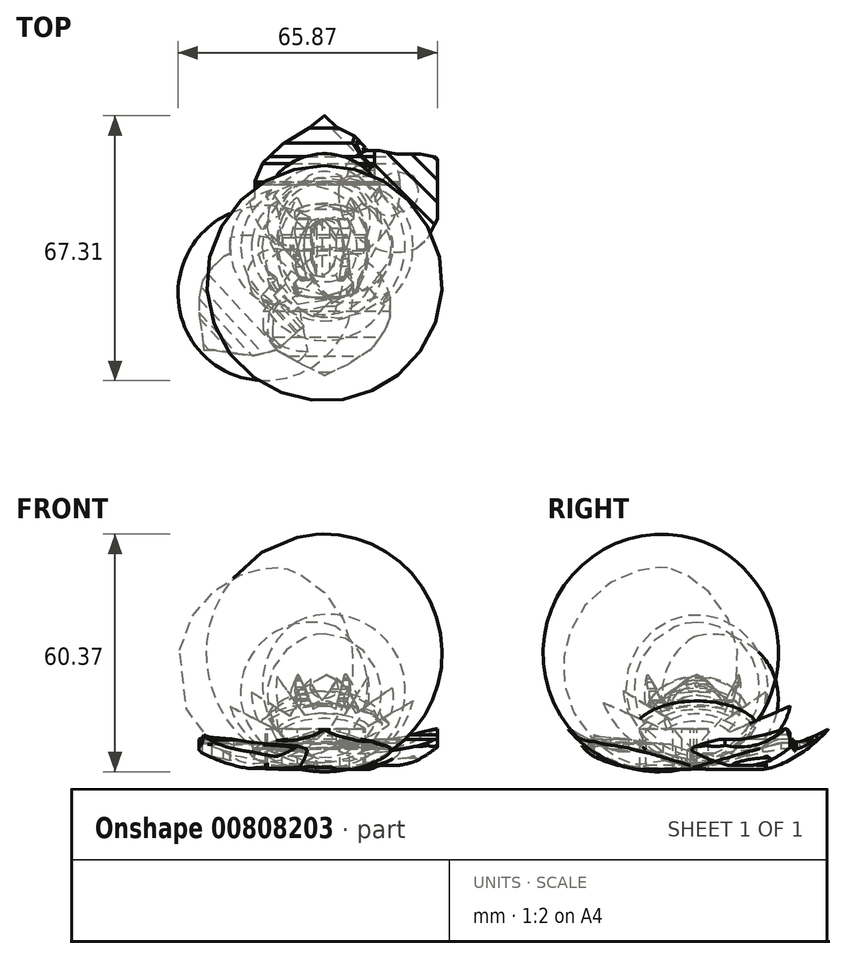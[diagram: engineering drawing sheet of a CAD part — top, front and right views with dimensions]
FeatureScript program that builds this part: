
annotation { "Feature Type Name" : "Feature", "Feature Type Description" : "" }
export const myFeature = defineFeature(function(context is Context, id is Id, definition is map)
    precondition{}
    {
        {
            var Q0;
            Q0=qCreatedBy(makeId("Front.planeOp"),FACE);
            var sketch = newSketch(context, id + "F0", { "sketchPlane" : qUnion([Q0])});
            skLineSegment(sketch, "E0", {"start": v(0, 14.2) * mm, "end": v(0, -5.34) * mm});
            skArc(sketch, "E1", {"start": v(0, -5.34) * mm, "mid": v(7.6, 4.43) * mm, "end": v(0, 14.2) * mm});
            skSolve(sketch);
        }
        {
            var Q0;
            Q0 = qSketchRegion(id + "F0", true);
            var Q1;
            Q1=sQuery(id+"F0.wireOp",EDGE,"E0");
            revolve(context, id + "F1", {"surfaceOperationType" : NewSurfaceOperationType.NEW, "entities" : qUnion([Q0]), "axis" : qUnion([Q1]), "revolveType" : RevolveType.FULL});
        }
        {
            var Q0;
            Q0=qCreatedBy(makeId("Front.planeOp"),FACE);
            var sketch = newSketch(context, id + "F2", { "sketchPlane" : qUnion([Q0])});
            skLineSegment(sketch, "E2", {"start": v(-1.74, 15.97) * mm, "end": v(-3.4, 13.54) * mm});
            skLineSegment(sketch, "E3", {"start": v(-3.4, 13.54) * mm, "end": v(-3.4, 11.38) * mm});
            skLineSegment(sketch, "E4", {"start": v(-3.4, 11.38) * mm, "end": v(-0.63, 7.29) * mm});
            skLineSegment(sketch, "E5", {"start": v(-0.63, 7.29) * mm, "end": v(1.25, 9.5) * mm});
            skLineSegment(sketch, "E6", {"start": v(1.25, 9.5) * mm, "end": v(2.98, 12.29) * mm});
            skLineSegment(sketch, "E7", {"start": v(2.98, 12.29) * mm, "end": v(2.98, 13.88) * mm});
            skLineSegment(sketch, "E8", {"start": v(2.98, 13.88) * mm, "end": v(2.29, 15.97) * mm});
            skLineSegment(sketch, "E9", {"start": v(2.29, 15.97) * mm, "end": v(-1.74, 15.97) * mm});
            skSolve(sketch);
        }
        {
            var Q0;
            Q0 = qSketchRegion(id + "F2", true);
            extrude(context, id + "F3", {"entities" : qUnion([Q0]), "operationType" : NewBodyOperationType.REMOVE, "oppositeDirection" : true, "depth" : 25.4 * mm, "offsetDistance" : 25.4 * mm});
        }
        {
            var Q0;
            Q0 = qSketchRegion(id + "F2", true);
            extrude(context, id + "F4", {"entities" : qUnion([Q0]), "operationType" : NewBodyOperationType.REMOVE, "depth" : 25.4 * mm, "offsetDistance" : 25.4 * mm});
        }
        {
            var Q0;
            Q0=qCreatedBy(makeId("Front.planeOp"),FACE);
            var sketch = newSketch(context, id + "F5", { "sketchPlane" : qUnion([Q0])});
            skLineSegment(sketch, "E10", {"start": v(2.63, 4.43) * mm, "end": v(8.5, 2.9) * mm});
            skArc(sketch, "E11", {"start": v(8.5, 2.9) * mm, "mid": v(8.02, 8.9) * mm, "end": v(5.25, 14.26) * mm});
            skLineSegment(sketch, "E12", {"start": v(5.25, 14.26) * mm, "end": v(2.63, 4.43) * mm});
            skSolve(sketch);
        }
        {
            var Q0;
            Q0 = qSketchRegion(id + "F5", true);
            var Q1;
            Q1=sQuery(id+"F5.wireOp",EDGE,"E10");
            revolve(context, id + "F6", {"operationType" : NewBodyOperationType.ADD, "surfaceOperationType" : NewSurfaceOperationType.NEW, "entities" : qUnion([Q0]), "axis" : qUnion([Q1]), "revolveType" : RevolveType.FULL});
        }
        {
            var Q0;
            Q0=qCreatedBy(makeId("Front.planeOp"),FACE);
            var sketch = newSketch(context, id + "F7", { "sketchPlane" : qUnion([Q0])});
            skLineSegment(sketch, "E13", {"start": v(-6.7, 13.9) * mm, "end": v(-1.32, 3.83) * mm});
            skLineSegment(sketch, "E14", {"start": v(-1.32, 3.83) * mm, "end": v(-7.78, 1.4) * mm});
            skArc(sketch, "E15", {"start": v(-6.7, 13.9) * mm, "mid": v(-8.72, 7.78) * mm, "end": v(-7.78, 1.4) * mm});
            skSolve(sketch);
        }
        {
            var Q0;
            Q0 = qSketchRegion(id + "F7", true);
            var Q1;
            Q1=sQuery(id+"F7.wireOp",EDGE,"E14");
            revolve(context, id + "F8", {"operationType" : NewBodyOperationType.ADD, "surfaceOperationType" : NewSurfaceOperationType.NEW, "entities" : qUnion([Q0]), "axis" : qUnion([Q1]), "revolveType" : RevolveType.FULL});
        }
        {
            var Q0;
            Q0=qCreatedBy(makeId("Front.planeOp"),FACE);
            var sketch = newSketch(context, id + "F9", { "sketchPlane" : qUnion([Q0])});
            skLineSegment(sketch, "E16", {"start": v(3.45, -3.75) * mm, "end": v(0, -5.55) * mm});
            skLineSegment(sketch, "E17", {"start": v(0, -5.55) * mm, "end": v(-1.31, -5.1) * mm});
            skLineSegment(sketch, "E18", {"start": v(-1.31, -5.1) * mm, "end": v(-2.95, -4.56) * mm});
            skLineSegment(sketch, "E19", {"start": v(-2.95, -4.56) * mm, "end": v(-4.9, -3.61) * mm});
            skLineSegment(sketch, "E20", {"start": v(-4.9, -3.61) * mm, "end": v(-4.41, -5.72) * mm});
            skLineSegment(sketch, "E21", {"start": v(-4.41, -5.72) * mm, "end": v(1, -7.97) * mm});
            skLineSegment(sketch, "E22", {"start": v(1, -7.97) * mm, "end": v(3.45, -3.75) * mm});
            skSolve(sketch);
        }
        {
            var Q0;
            Q0 = qSketchRegion(id + "F9", true);
            extrude(context, id + "F10", {"entities" : qUnion([Q0]), "operationType" : NewBodyOperationType.REMOVE, "oppositeDirection" : true, "depth" : 25.4 * mm, "offsetDistance" : 25.4 * mm});
        }
        {
            var Q0;
            Q0 = qSketchRegion(id + "F9", true);
            extrude(context, id + "F11", {"entities" : qUnion([Q0]), "operationType" : NewBodyOperationType.REMOVE, "depth" : 25.4 * mm, "offsetDistance" : 25.4 * mm});
        }
        {
            var Q0;
            Q0=qCreatedBy(makeId("Right.planeOp"),FACE);
            var sketch = newSketch(context, id + "F12", { "sketchPlane" : qUnion([Q0])});
            skLineSegment(sketch, "E23", {"start": v(0, -5.52) * mm, "end": v(-12.6, 14.04) * mm});
            skLineSegment(sketch, "E24", {"start": v(-12.6, 14.04) * mm, "end": v(-5.19, 2.53) * mm});
            skLineSegment(sketch, "E25", {"start": v(-5.19, 2.53) * mm, "end": v(-11.6, 0) * mm});
            skArc(sketch, "E26", {"start": v(-12.6, 14.04) * mm, "mid": v(-13.1, 6.95) * mm, "end": v(-11.6, 0) * mm});
            skSolve(sketch);
        }
        {
            var Q0;
            Q0=qCreatedBy(makeId("Right.planeOp"),FACE);
            var sketch = newSketch(context, id + "F13", { "sketchPlane" : qUnion([Q0])});
            skLineSegment(sketch, "E27", {"start": v(0.52, 17) * mm, "end": v(1.55, 15.39) * mm});
            skLineSegment(sketch, "E28", {"start": v(1.55, 15.39) * mm, "end": v(4.15, 13.96) * mm});
            skLineSegment(sketch, "E29", {"start": v(4.15, 13.96) * mm, "end": v(8.05, 11.22) * mm});
            skLineSegment(sketch, "E30", {"start": v(8.05, 11.22) * mm, "end": v(9.5, 7.76) * mm});
            skLineSegment(sketch, "E31", {"start": v(9.5, 7.76) * mm, "end": v(9.5, 5.02) * mm});
            skLineSegment(sketch, "E32", {"start": v(9.5, 5.02) * mm, "end": v(9.5, 2.03) * mm});
            skLineSegment(sketch, "E33", {"start": v(9.5, 2.03) * mm, "end": v(8.62, 0) * mm});
            skLineSegment(sketch, "E34", {"start": v(8.62, 0) * mm, "end": v(6.68, -2.62) * mm});
            skLineSegment(sketch, "E35", {"start": v(6.68, -2.62) * mm, "end": v(1.83, -5.49) * mm});
            skLineSegment(sketch, "E36", {"start": v(1.83, -5.49) * mm, "end": v(0.67, -5.49) * mm});
            skLineSegment(sketch, "E37", {"start": v(0.67, -5.49) * mm, "end": v(5.65, -6.91) * mm});
            skLineSegment(sketch, "E38", {"start": v(5.65, -6.91) * mm, "end": v(12.66, -3.5) * mm});
            skLineSegment(sketch, "E39", {"start": v(12.66, -3.5) * mm, "end": v(12.66, 2.12) * mm});
            skLineSegment(sketch, "E40", {"start": v(12.66, 2.12) * mm, "end": v(11.25, 16) * mm});
            skLineSegment(sketch, "E41", {"start": v(11.25, 16) * mm, "end": v(0.52, 17) * mm});
            skSolve(sketch);
        }
        {
            var Q0;
            Q0 = qSketchRegion(id + "F13", true);
            extrude(context, id + "F14", {"entities" : qUnion([Q0]), "operationType" : NewBodyOperationType.REMOVE, "depth" : 25.4 * mm, "offsetDistance" : 25.4 * mm});
        }
        {
            var Q0;
            Q0 = qSketchRegion(id + "F13", true);
            extrude(context, id + "F15", {"entities" : qUnion([Q0]), "operationType" : NewBodyOperationType.REMOVE, "oppositeDirection" : true, "depth" : 25.4 * mm, "offsetDistance" : 25.4 * mm});
        }
        {
            var Q0;
            Q0=qCreatedBy(makeId("Right.planeOp"),FACE);
            var sketch = newSketch(context, id + "F16", { "sketchPlane" : qUnion([Q0])});
            skLineSegment(sketch, "E42", {"start": v(0, 14.33) * mm, "end": v(3.36, 12.86) * mm});
            skLineSegment(sketch, "E43", {"start": v(3.36, 12.86) * mm, "end": v(5.83, 10.3) * mm});
            skLineSegment(sketch, "E44", {"start": v(5.83, 10.3) * mm, "end": v(7.11, 7.74) * mm});
            skLineSegment(sketch, "E45", {"start": v(7.11, 7.74) * mm, "end": v(8.3, 4.27) * mm});
            skLineSegment(sketch, "E46", {"start": v(8.3, 4.27) * mm, "end": v(6.93, 0.98) * mm});
            skLineSegment(sketch, "E47", {"start": v(6.93, 0.98) * mm, "end": v(5, -1.22) * mm});
            skLineSegment(sketch, "E48", {"start": v(5, -1.22) * mm, "end": v(1.17, -5.06) * mm});
            skLineSegment(sketch, "E49", {"start": v(1.17, -5.06) * mm, "end": v(0, -6.16) * mm});
            skLineSegment(sketch, "E50", {"start": v(0, -6.16) * mm, "end": v(3.18, -7.71) * mm});
            skLineSegment(sketch, "E51", {"start": v(3.18, -7.71) * mm, "end": v(12.6, 0) * mm});
            skLineSegment(sketch, "E52", {"start": v(12.6, 0) * mm, "end": v(12.6, 9.2) * mm});
            skLineSegment(sketch, "E53", {"start": v(12.6, 9.2) * mm, "end": v(8.12, 14.14) * mm});
            skLineSegment(sketch, "E54", {"start": v(8.12, 14.14) * mm, "end": v(0, 14.33) * mm});
            skSolve(sketch);
        }
        {
            var Q0;
            Q0 = qSketchRegion(id + "F16", true);
            extrude(context, id + "F17", {"entities" : qUnion([Q0]), "operationType" : NewBodyOperationType.REMOVE, "oppositeDirection" : true, "depth" : 25.4 * mm, "offsetDistance" : 25.4 * mm});
        }
        {
            var Q0;
            Q0 = qSketchRegion(id + "F16", true);
            extrude(context, id + "F18", {"entities" : qUnion([Q0]), "operationType" : NewBodyOperationType.REMOVE, "depth" : 25.4 * mm, "offsetDistance" : 25.4 * mm});
        }
        {
            var Q0;
            Q0=qCreatedBy(makeId("Right.planeOp"),FACE);
            var sketch = newSketch(context, id + "F19", { "sketchPlane" : qUnion([Q0])});
            skLineSegment(sketch, "E55", {"start": v(0, 14.92) * mm, "end": v(-4.7, 12.16) * mm});
            skLineSegment(sketch, "E56", {"start": v(-4.7, 12.16) * mm, "end": v(-7.9, 8.97) * mm});
            skLineSegment(sketch, "E57", {"start": v(-7.9, 8.97) * mm, "end": v(-8.9, 6.06) * mm});
            skLineSegment(sketch, "E58", {"start": v(-8.9, 6.06) * mm, "end": v(-8.9, 1.85) * mm});
            skLineSegment(sketch, "E59", {"start": v(-8.9, 1.85) * mm, "end": v(-7.3, -1.78) * mm});
            skLineSegment(sketch, "E60", {"start": v(-7.3, -1.78) * mm, "end": v(-3.53, -5.7) * mm});
            skLineSegment(sketch, "E61", {"start": v(-3.53, -5.7) * mm, "end": v(-1.5, -6.86) * mm});
            skLineSegment(sketch, "E62", {"start": v(-1.5, -6.86) * mm, "end": v(-6.3, -10.64) * mm});
            skLineSegment(sketch, "E63", {"start": v(-6.3, -10.64) * mm, "end": v(-15.88, -2.5) * mm});
            skLineSegment(sketch, "E64", {"start": v(-15.88, -2.5) * mm, "end": v(-15.88, 6.06) * mm});
            skLineSegment(sketch, "E65", {"start": v(-15.88, 6.06) * mm, "end": v(-5.86, 16.08) * mm});
            skLineSegment(sketch, "E66", {"start": v(-5.86, 16.08) * mm, "end": v(0, 14.92) * mm});
            skSolve(sketch);
        }
        {
            var Q0;
            Q0 = qSketchRegion(id + "F19", true);
            extrude(context, id + "F20", {"entities" : qUnion([Q0]), "operationType" : NewBodyOperationType.REMOVE, "oppositeDirection" : true, "depth" : 25.4 * mm, "offsetDistance" : 25.4 * mm});
        }
        {
            var Q0;
            Q0 = qSketchRegion(id + "F19", true);
            extrude(context, id + "F21", {"entities" : qUnion([Q0]), "operationType" : NewBodyOperationType.REMOVE, "depth" : 25.4 * mm, "offsetDistance" : 25.4 * mm});
        }
        {
            var Q0;
            Q0=qCreatedBy(makeId("Right.planeOp"),FACE);
            var sketch = newSketch(context, id + "F22", { "sketchPlane" : qUnion([Q0])});
            skLineSegment(sketch, "E67", {"start": v(0, 14.3) * mm, "end": v(0, 13.37) * mm});
            skLineSegment(sketch, "E68", {"start": v(4.66, 10.12) * mm, "end": v(7.1, 7.8) * mm});
            skLineSegment(sketch, "E69", {"start": v(7.1, 7.8) * mm, "end": v(9.19, 6.75) * mm});
            skLineSegment(sketch, "E70", {"start": v(9.19, 6.75) * mm, "end": v(4.78, 22.54) * mm});
            skLineSegment(sketch, "E71", {"start": v(-7.42, 16.04) * mm, "end": v(-10.43, 7.33) * mm});
            skLineSegment(sketch, "E72", {"start": v(-10.43, 7.33) * mm, "end": v(-7.65, 8.96) * mm});
            skLineSegment(sketch, "E73", {"start": v(4.66, 10.12) * mm, "end": v(2.6, 12.38) * mm});
            skLineSegment(sketch, "E74", {"start": v(2.6, 12.38) * mm, "end": v(1.43, 13.03) * mm});
            skLineSegment(sketch, "E75", {"start": v(1.43, 13.03) * mm, "end": v(0, 13.83) * mm});
            skLineSegment(sketch, "E76", {"start": v(0, 13.83) * mm, "end": v(-1.9, 12.9) * mm});
            skLineSegment(sketch, "E77", {"start": v(-1.9, 12.9) * mm, "end": v(-3.08, 12.3) * mm});
            skLineSegment(sketch, "E78", {"start": v(-3.08, 12.3) * mm, "end": v(-4.97, 10.7) * mm});
            skLineSegment(sketch, "E79", {"start": v(-4.97, 10.7) * mm, "end": v(-7.65, 8.96) * mm});
            skLineSegment(sketch, "E80", {"start": v(4.78, 22.54) * mm, "end": v(-7.42, 16.04) * mm});
            skSolve(sketch);
        }
        {
            var Q0;
            Q0 = qSketchRegion(id + "F22", true);
            extrude(context, id + "F23", {"entities" : qUnion([Q0]), "operationType" : NewBodyOperationType.REMOVE, "oppositeDirection" : true, "depth" : 25.4 * mm, "offsetDistance" : 25.4 * mm});
        }
        {
            var Q0;
            Q0 = qSketchRegion(id + "F22", true);
            extrude(context, id + "F24", {"entities" : qUnion([Q0]), "operationType" : NewBodyOperationType.REMOVE, "depth" : 25.4 * mm, "offsetDistance" : 25.4 * mm});
        }
        {
            var Q0;
            Q0 = qSketchRegion(id + "F12", true);
            var Q1;
            Q1=sQuery(id+"F12.wireOp",EDGE,"E25");
            revolve(context, id + "F25", {"operationType" : NewBodyOperationType.ADD, "surfaceOperationType" : NewSurfaceOperationType.NEW, "entities" : qUnion([Q0]), "axis" : qUnion([Q1]), "revolveType" : RevolveType.FULL});
        }
        {
            var Q0;
            Q0=qCreatedBy(makeId("Right.planeOp"),FACE);
            var sketch = newSketch(context, id + "F26", { "sketchPlane" : qUnion([Q0])});
            skLineSegment(sketch, "E81", {"start": v(-3.39, -5.78) * mm, "end": v(-7.85, -2.14) * mm});
            skLineSegment(sketch, "E82", {"start": v(-7.85, -2.14) * mm, "end": v(-10.74, 1.63) * mm});
            skLineSegment(sketch, "E83", {"start": v(-10.74, 1.63) * mm, "end": v(-13.28, 6.92) * mm});
            skLineSegment(sketch, "E84", {"start": v(-13.28, 6.92) * mm, "end": v(-14.03, 9.12) * mm});
            skLineSegment(sketch, "E85", {"start": v(-14.03, 9.12) * mm, "end": v(-11.08, -14.57) * mm});
            skLineSegment(sketch, "E86", {"start": v(-11.08, -14.57) * mm, "end": v(1.97, -13.61) * mm});
            skLineSegment(sketch, "E87", {"start": v(1.97, -13.61) * mm, "end": v(-3.39, -5.78) * mm});
            skSolve(sketch);
        }
        {
            var Q0;
            Q0 = qSketchRegion(id + "F26", true);
            extrude(context, id + "F27", {"entities" : qUnion([Q0]), "operationType" : NewBodyOperationType.REMOVE, "oppositeDirection" : true, "depth" : 25.4 * mm, "offsetDistance" : 25.4 * mm});
        }
        {
            var Q0;
            Q0 = qSketchRegion(id + "F26", true);
            extrude(context, id + "F28", {"entities" : qUnion([Q0]), "operationType" : NewBodyOperationType.REMOVE, "depth" : 25.4 * mm, "offsetDistance" : 25.4 * mm});
        }
        {
            var Q0;
            Q0=qCreatedBy(makeId("Front.planeOp"),FACE);
            var sketch = newSketch(context, id + "F29", { "sketchPlane" : qUnion([Q0])});
            skLineSegment(sketch, "E88", {"start": v(-4.45, -3.98) * mm, "end": v(-8.33, 0.69) * mm});
            skLineSegment(sketch, "E89", {"start": v(-8.33, 0.69) * mm, "end": v(-9.36, 4.62) * mm});
            skLineSegment(sketch, "E90", {"start": v(-9.36, 4.62) * mm, "end": v(-9.36, 7.83) * mm});
            skLineSegment(sketch, "E91", {"start": v(-9.36, 7.83) * mm, "end": v(-8.33, 10.44) * mm});
            skLineSegment(sketch, "E92", {"start": v(-8.33, 10.44) * mm, "end": v(-8.17, 10.65) * mm});
            skLineSegment(sketch, "E93", {"start": v(-8.17, 10.65) * mm, "end": v(-7.8, 11.73) * mm});
            skLineSegment(sketch, "E94", {"start": v(-7.8, 11.73) * mm, "end": v(-7.87, 12.2) * mm});
            skLineSegment(sketch, "E95", {"start": v(-7.87, 12.2) * mm, "end": v(-6.8, 15.32) * mm});
            skLineSegment(sketch, "E96", {"start": v(-6.8, 15.32) * mm, "end": v(4.49, 16.52) * mm});
            skLineSegment(sketch, "E97", {"start": v(4.49, 16.52) * mm, "end": v(6.8, 12.38) * mm});
            skLineSegment(sketch, "E98", {"start": v(6.8, 12.38) * mm, "end": v(7.27, 11.02) * mm});
            skLineSegment(sketch, "E99", {"start": v(7.27, 11.02) * mm, "end": v(7.8, 10.08) * mm});
            skLineSegment(sketch, "E100", {"start": v(7.8, 10.08) * mm, "end": v(8.68, 8.5) * mm});
            skLineSegment(sketch, "E101", {"start": v(8.68, 8.5) * mm, "end": v(9.3, 5.4) * mm});
            skLineSegment(sketch, "E102", {"start": v(9.3, 5.4) * mm, "end": v(9.3, 2.58) * mm});
            skLineSegment(sketch, "E103", {"start": v(9.3, 2.58) * mm, "end": v(7.8, 0) * mm});
            skLineSegment(sketch, "E104", {"start": v(7.8, 0) * mm, "end": v(5.75, -2.67) * mm});
            skLineSegment(sketch, "E105", {"start": v(2.57, -6.94) * mm, "end": v(17.93, -6.36) * mm});
            skLineSegment(sketch, "E106", {"start": v(17.93, -6.36) * mm, "end": v(16.64, 5.4) * mm});
            skLineSegment(sketch, "E107", {"start": v(16.64, 5.4) * mm, "end": v(7.47, 19.86) * mm});
            skLineSegment(sketch, "E108", {"start": v(7.47, 19.86) * mm, "end": v(-7.7, 19.86) * mm});
            skLineSegment(sketch, "E109", {"start": v(-7.7, 19.86) * mm, "end": v(-17.32, 9.98) * mm});
            skLineSegment(sketch, "E110", {"start": v(-17.32, 9.98) * mm, "end": v(-17.32, -5.61) * mm});
            skLineSegment(sketch, "E111", {"start": v(-17.32, -5.61) * mm, "end": v(-0.53, -6.87) * mm});
            skLineSegment(sketch, "E112", {"start": v(5.75, -2.67) * mm, "end": v(3.27, -3.92) * mm});
            skLineSegment(sketch, "E113", {"start": v(3.27, -3.92) * mm, "end": v(1.22, -5.09) * mm});
            skLineSegment(sketch, "E114", {"start": v(1.22, -5.09) * mm, "end": v(0, -5.65) * mm});
            skLineSegment(sketch, "E115", {"start": v(0, -5.65) * mm, "end": v(0, -6.34) * mm});
            skLineSegment(sketch, "E116", {"start": v(-4.45, -3.98) * mm, "end": v(-3.6, -4.44) * mm});
            skLineSegment(sketch, "E117", {"start": v(-3.6, -4.44) * mm, "end": v(-1.15, -5.3) * mm});
            skLineSegment(sketch, "E118", {"start": v(-1.15, -5.3) * mm, "end": v(-0.17, -5.56) * mm});
            skLineSegment(sketch, "E119", {"start": v(-0.17, -5.56) * mm, "end": v(-0.4, -6.42) * mm});
            skLineSegment(sketch, "E120", {"start": v(0, -6.34) * mm, "end": v(2.57, -6.94) * mm});
            skLineSegment(sketch, "E121", {"start": v(-0.4, -6.42) * mm, "end": v(-0.53, -6.87) * mm});
            skSolve(sketch);
        }
        {
            var Q0;
            Q0 = qSketchRegion(id + "F29", true);
            extrude(context, id + "F30", {"entities" : qUnion([Q0]), "operationType" : NewBodyOperationType.REMOVE, "depth" : 25.4 * mm, "offsetDistance" : 25.4 * mm});
        }
        {
            var Q0;
            Q0 = qSketchRegion(id + "F29", true);
            extrude(context, id + "F31", {"entities" : qUnion([Q0]), "operationType" : NewBodyOperationType.REMOVE, "oppositeDirection" : true, "depth" : 25.4 * mm, "offsetDistance" : 25.4 * mm});
        }
        {
            var Q0;
            Q0=qCreatedBy(makeId("Right.planeOp"),FACE);
            var sketch = newSketch(context, id + "F32", { "sketchPlane" : qUnion([Q0])});
            skLineSegment(sketch, "E122", {"start": v(-8.5, 7.64) * mm, "end": v(-8.5, 18.96) * mm});
            skSolve(sketch);
        }
        {
            var Q0;
            Q0=makeQuery(id+"F21.boolean.opBoolean","INTERSECT",EDGE,{"derivedFrom":[makeQuery(id+"F6.opRevolve","SWEPT_FACE",FACE,{"disambiguationData":[OSD([sQuery(id+"F5.wireOp",EDGE,"E12")])]}),makeQuery(id+"F21.opExtrude","SWEPT_FACE",FACE,{"disambiguationData":[OSD([sQuery(id+"F19.wireOp",EDGE,"E57")])]})]});
            cPoint(context, id + "F33", {"entities" : qUnion([Q0]), "parameter" : 0.5});
        }
        {
            var Q0;
            Q0=sQuery(id+"F32.wireOp",EDGE,"E122");
            var Q1;
            Q1 = qCreatedBy(id + "F33" ,VERTEX);
            cPlane(context, id + "F34", {"entities" : qUnion([Q0, Q1]), "cplaneType" : CPlaneType.LINE_ANGLE, "offset" : 25.4 * mm, "angle" : 0 * degree, "width" : 152.4 * mm, "height" : 152.4 * mm});
        }
        {
            var Q0;
            Q0=qCreatedBy(id+"F34.planeOp",FACE);
            var sketch = newSketch(context, id + "F35", { "sketchPlane" : qUnion([Q0])});
            skLineSegment(sketch, "E123", {"start": v(-9, 4.8) * mm, "end": v(-9, 11.2) * mm});
            skLineSegment(sketch, "E124", {"start": v(-9, 11.2) * mm, "end": v(0.67, 16.9) * mm});
            skLineSegment(sketch, "E125", {"start": v(0.67, 16.9) * mm, "end": v(13.04, 9.66) * mm});
            skLineSegment(sketch, "E126", {"start": v(13.04, 9.66) * mm, "end": v(11.08, 0.58) * mm});
            skLineSegment(sketch, "E127", {"start": v(11.08, 0.58) * mm, "end": v(10.13, 1.93) * mm});
            skLineSegment(sketch, "E128", {"start": v(10.13, 1.93) * mm, "end": v(9.59, 1) * mm});
            skLineSegment(sketch, "E129", {"start": v(9.59, 1) * mm, "end": v(9.59, 3.21) * mm});
            skLineSegment(sketch, "E130", {"start": v(9.59, 3.21) * mm, "end": v(9.59, 4.84) * mm});
            skLineSegment(sketch, "E131", {"start": v(9.59, 4.84) * mm, "end": v(8.5, 6.85) * mm});
            skLineSegment(sketch, "E132", {"start": v(8.5, 6.85) * mm, "end": v(7.55, 9.66) * mm});
            skLineSegment(sketch, "E133", {"start": v(7.55, 9.66) * mm, "end": v(5.07, 11.1) * mm});
            skLineSegment(sketch, "E134", {"start": v(5.07, 11.1) * mm, "end": v(2.05, 12.87) * mm});
            skLineSegment(sketch, "E135", {"start": v(2.05, 12.87) * mm, "end": v(0.53, 13.76) * mm});
            skLineSegment(sketch, "E136", {"start": v(0.53, 13.76) * mm, "end": v(-1.27, 12.9) * mm});
            skLineSegment(sketch, "E137", {"start": v(-1.27, 12.9) * mm, "end": v(-2.96, 11.95) * mm});
            skLineSegment(sketch, "E138", {"start": v(-2.96, 11.95) * mm, "end": v(-4.87, 10.27) * mm});
            skLineSegment(sketch, "E139", {"start": v(-4.87, 10.27) * mm, "end": v(-5.81, 8.65) * mm});
            skLineSegment(sketch, "E140", {"start": v(-5.81, 8.65) * mm, "end": v(-7.24, 6.22) * mm});
            skLineSegment(sketch, "E141", {"start": v(-7.24, 6.22) * mm, "end": v(-8.62, 3.85) * mm});
            skLineSegment(sketch, "E142", {"start": v(-8.62, 3.85) * mm, "end": v(-9.31, 2.67) * mm});
            skLineSegment(sketch, "E143", {"start": v(-9.31, 2.67) * mm, "end": v(-9, 4.8) * mm});
            skSolve(sketch);
        }
        {
            var Q0;
            Q0 = qSketchRegion(id + "F35", true);
            extrude(context, id + "F36", {"entities" : qUnion([Q0]), "operationType" : NewBodyOperationType.REMOVE, "oppositeDirection" : true, "depth" : 25.4 * mm, "offsetDistance" : 25.4 * mm});
        }
        {
            var Q0;
            Q0 = qSketchRegion(id + "F35", true);
            extrude(context, id + "F37", {"entities" : qUnion([Q0]), "operationType" : NewBodyOperationType.REMOVE, "depth" : 0.64 * mm, "offsetDistance" : 25.4 * mm});
        }
        {
            var Q0;
            Q0=qCreatedBy(makeId("Right.planeOp"),FACE);
            var sketch = newSketch(context, id + "F38", { "sketchPlane" : qUnion([Q0])});
            skLineSegment(sketch, "E144", {"start": v(1.13, -5.26) * mm, "end": v(10.6, 13.87) * mm});
            skLineSegment(sketch, "E145", {"start": v(5.86, 4.3) * mm, "end": v(8.9, 2.8) * mm});
            skArc(sketch, "E146", {"start": v(8.9, 2.8) * mm, "mid": v(11, 8.15) * mm, "end": v(10.6, 13.87) * mm});
            skSolve(sketch);
        }
        {
            var Q0;
            Q0 = qSketchRegion(id + "F38", true);
            var Q1;
            Q1=sQuery(id+"F38.wireOp",EDGE,"E145");
            revolve(context, id + "F39", {"operationType" : NewBodyOperationType.ADD, "surfaceOperationType" : NewSurfaceOperationType.NEW, "entities" : qUnion([Q0]), "axis" : qUnion([Q1]), "revolveType" : RevolveType.FULL});
        }
        {
            var Q0;
            Q0=qCreatedBy(makeId("Right.planeOp"),FACE);
            var sketch = newSketch(context, id + "F40", { "sketchPlane" : qUnion([Q0])});
            skLineSegment(sketch, "E147", {"start": v(7.27, 4.1) * mm, "end": v(7.27, 20.28) * mm});
            skSolve(sketch);
        }
        {
            var Q0;
            Q0=sQuery(id+"F40.wireOp",EDGE,"E147");
            var Q1;
            Q1=qCreatedBy(makeId("Front.planeOp"),FACE);
            cPlane(context, id + "F41", {"entities" : qUnion([Q0, Q1]), "cplaneType" : CPlaneType.LINE_ANGLE, "offset" : 25.4 * mm, "angle" : 0 * degree, "width" : 152.4 * mm, "height" : 152.4 * mm});
        }
        {
            var Q0;
            Q0=qCreatedBy(id+"F41.planeOp",FACE);
            var sketch = newSketch(context, id + "F42", { "sketchPlane" : qUnion([Q0])});
            skLineSegment(sketch, "E148", {"start": v(-0.6, -5.5) * mm, "end": v(-5.76, -2.67) * mm});
            skLineSegment(sketch, "E149", {"start": v(-5.76, -2.67) * mm, "end": v(-7.8, 0) * mm});
            skLineSegment(sketch, "E150", {"start": v(-7.8, 0) * mm, "end": v(-9.33, 2.6) * mm});
            skLineSegment(sketch, "E151", {"start": v(-9.33, 2.6) * mm, "end": v(-9.33, 4.2) * mm});
            skLineSegment(sketch, "E152", {"start": v(-9.33, 4.2) * mm, "end": v(-5.76, 10.37) * mm});
            skLineSegment(sketch, "E153", {"start": v(-5.76, 10.37) * mm, "end": v(-4.11, 11.79) * mm});
            skLineSegment(sketch, "E154", {"start": v(-4.11, 11.79) * mm, "end": v(-0.6, 13.71) * mm});
            skLineSegment(sketch, "E155", {"start": v(-0.6, 13.71) * mm, "end": v(6.48, 9.8) * mm});
            skLineSegment(sketch, "E156", {"start": v(6.48, 9.8) * mm, "end": v(7.62, 6.63) * mm});
            skLineSegment(sketch, "E157", {"start": v(7.62, 6.63) * mm, "end": v(8.75, 4.64) * mm});
            skLineSegment(sketch, "E158", {"start": v(8.75, 4.64) * mm, "end": v(8.75, 2.66) * mm});
            skLineSegment(sketch, "E159", {"start": v(8.75, 2.66) * mm, "end": v(8.35, 0.73) * mm});
            skLineSegment(sketch, "E160", {"start": v(8.35, 0.73) * mm, "end": v(4.33, -4.14) * mm});
            skLineSegment(sketch, "E161", {"start": v(4.33, -4.14) * mm, "end": v(0, -5.67) * mm});
            skLineSegment(sketch, "E162", {"start": v(0, -5.67) * mm, "end": v(0.4, -6.8) * mm});
            skLineSegment(sketch, "E163", {"start": v(0.4, -6.8) * mm, "end": v(10.57, -3.22) * mm});
            skLineSegment(sketch, "E164", {"start": v(10.57, -3.22) * mm, "end": v(11.36, 13.09) * mm});
            skLineSegment(sketch, "E165", {"start": v(11.36, 13.09) * mm, "end": v(3.2, 17.68) * mm});
            skLineSegment(sketch, "E166", {"start": v(3.2, 17.68) * mm, "end": v(-9.22, 16.32) * mm});
            skLineSegment(sketch, "E167", {"start": v(-9.22, 16.32) * mm, "end": v(-13.58, 5.27) * mm});
            skLineSegment(sketch, "E168", {"start": v(-13.58, 5.27) * mm, "end": v(-6.78, -6) * mm});
            skLineSegment(sketch, "E169", {"start": v(-6.78, -6) * mm, "end": v(-0.71, -6.92) * mm});
            skLineSegment(sketch, "E170", {"start": v(-0.71, -6.92) * mm, "end": v(-0.6, -5.5) * mm});
            skSolve(sketch);
        }
        {
            var Q0;
            Q0 = qSketchRegion(id + "F42", true);
            extrude(context, id + "F43", {"entities" : qUnion([Q0]), "operationType" : NewBodyOperationType.REMOVE, "depth" : 25.4 * mm, "offsetDistance" : 25.4 * mm});
        }
        {
            var Q0;
            Q0=qCreatedBy(makeId("Front.planeOp"),FACE);
            var sketch = newSketch(context, id + "F44", { "sketchPlane" : qUnion([Q0])});
            skLineSegment(sketch, "E171", {"start": v(-8.2, 0) * mm, "end": v(-4.4, -4.04) * mm});
            skLineSegment(sketch, "E172", {"start": v(-4.4, -4.04) * mm, "end": v(-1.5, -5.33) * mm});
            skLineSegment(sketch, "E173", {"start": v(-1.5, -5.33) * mm, "end": v(-2.35, -5.78) * mm});
            skLineSegment(sketch, "E174", {"start": v(-2.35, -5.78) * mm, "end": v(-8.77, -3.2) * mm});
            skLineSegment(sketch, "E175", {"start": v(-8.77, -3.2) * mm, "end": v(-13.32, 5.96) * mm});
            skLineSegment(sketch, "E176", {"start": v(-13.32, 5.96) * mm, "end": v(-10.38, 13.76) * mm});
            skLineSegment(sketch, "E177", {"start": v(-10.38, 13.76) * mm, "end": v(-5.2, 15.68) * mm});
            skLineSegment(sketch, "E178", {"start": v(-5.2, 15.68) * mm, "end": v(9.12, 15.5) * mm});
            skLineSegment(sketch, "E179", {"start": v(-8.8, 8.15) * mm, "end": v(-8.8, 13.05) * mm});
            skLineSegment(sketch, "E180", {"start": v(-8.8, 13.05) * mm, "end": v(-5.42, 14.83) * mm});
            skLineSegment(sketch, "E181", {"start": v(-5.42, 14.83) * mm, "end": v(8.05, 14.67) * mm});
            skLineSegment(sketch, "E182", {"start": v(8.05, 14.67) * mm, "end": v(8.54, 6.4) * mm});
            skLineSegment(sketch, "E183", {"start": v(8.54, 6.4) * mm, "end": v(8.54, 3.6) * mm});
            skLineSegment(sketch, "E184", {"start": v(8.54, 3.6) * mm, "end": v(8.18, 0.91) * mm});
            skLineSegment(sketch, "E185", {"start": v(8.18, 0.91) * mm, "end": v(5.86, -2.7) * mm});
            skLineSegment(sketch, "E186", {"start": v(5.86, -2.7) * mm, "end": v(1.54, -5.02) * mm});
            skLineSegment(sketch, "E187", {"start": v(1.54, -5.02) * mm, "end": v(0.64, -5.35) * mm});
            skLineSegment(sketch, "E188", {"start": v(0.64, -5.35) * mm, "end": v(5.82, -5.41) * mm});
            skLineSegment(sketch, "E189", {"start": v(5.82, -5.41) * mm, "end": v(15.19, 2.03) * mm});
            skLineSegment(sketch, "E190", {"start": v(15.19, 2.03) * mm, "end": v(9.12, 15.5) * mm});
            skLineSegment(sketch, "E191", {"start": v(-8.8, 8.15) * mm, "end": v(-8.46, 5.24) * mm});
            skLineSegment(sketch, "E192", {"start": v(-8.46, 5.24) * mm, "end": v(-8.46, 2.78) * mm});
            skLineSegment(sketch, "E193", {"start": v(-8.46, 2.78) * mm, "end": v(-7.79, 0) * mm});
            skLineSegment(sketch, "E194", {"start": v(-7.79, 0) * mm, "end": v(-7.32, -0.92) * mm});
            skSolve(sketch);
        }
        {
            var Q0;
            Q0 = qSketchRegion(id + "F44", true);
            extrude(context, id + "F45", {"entities" : qUnion([Q0]), "operationType" : NewBodyOperationType.REMOVE, "oppositeDirection" : true, "depth" : 25.4 * mm, "offsetDistance" : 25.4 * mm});
        }
        {
            var Q0;
            Q0 = qSketchRegion(id + "F44", true);
            extrude(context, id + "F46", {"entities" : qUnion([Q0]), "operationType" : NewBodyOperationType.REMOVE, "depth" : 25.4 * mm, "offsetDistance" : 25.4 * mm});
        }
        {
            var Q0;
            Q0=qCreatedBy(id+"F34.planeOp",FACE);
            var sketch = newSketch(context, id + "F47", { "sketchPlane" : qUnion([Q0])});
            skLineSegment(sketch, "E195", {"start": v(8.05, 7.27) * mm, "end": v(8.05, 5.36) * mm});
            skLineSegment(sketch, "E196", {"start": v(8.05, 5.36) * mm, "end": v(8.05, 3.6) * mm});
            skLineSegment(sketch, "E197", {"start": v(8.05, 3.6) * mm, "end": v(8.05, 1.28) * mm});
            skLineSegment(sketch, "E198", {"start": v(8.05, 1.28) * mm, "end": v(8.05, -1.97) * mm});
            skLineSegment(sketch, "E199", {"start": v(8.05, -1.97) * mm, "end": v(10.54, 4.22) * mm});
            skLineSegment(sketch, "E200", {"start": v(10.54, 4.22) * mm, "end": v(8.05, 7.27) * mm});
            skSolve(sketch);
        }
        {
            var Q0;
            Q0 = qSketchRegion(id + "F47", true);
            extrude(context, id + "F48", {"entities" : qUnion([Q0]), "operationType" : NewBodyOperationType.REMOVE, "depth" : 2.54 * mm, "offsetDistance" : 25.4 * mm});
        }
        {
            var Q0;
            Q0 = qSketchRegion(id + "F47", true);
            extrude(context, id + "F49", {"entities" : qUnion([Q0]), "operationType" : NewBodyOperationType.REMOVE, "oppositeDirection" : true, "depth" : 25.4 * mm, "offsetDistance" : 25.4 * mm});
        }
        {
            var Q0;
            Q0=qCreatedBy(makeId("Front.planeOp"),FACE);
            var sketch = newSketch(context, id + "F50", { "sketchPlane" : qUnion([Q0])});
            skLineSegment(sketch, "E201", {"start": v(-3.47, 1.27) * mm, "end": v(-12.04, 13.39) * mm});
            skLineSegment(sketch, "E202", {"start": v(-4.33, 2.49) * mm, "end": v(-9.1, -0.89) * mm});
            skArc(sketch, "E203", {"start": v(-12.04, 13.39) * mm, "mid": v(-11.79, 6) * mm, "end": v(-9.1, -0.89) * mm});
            skSolve(sketch);
        }
        {
            var Q0;
            Q0 = qSketchRegion(id + "F50", true);
            var Q1;
            Q1=sQuery(id+"F50.wireOp",EDGE,"E202");
            revolve(context, id + "F51", {"operationType" : NewBodyOperationType.ADD, "surfaceOperationType" : NewSurfaceOperationType.NEW, "entities" : qUnion([Q0]), "axis" : qUnion([Q1]), "revolveType" : RevolveType.FULL});
        }
        {
            var Q0;
            Q0=qCreatedBy(makeId("Front.planeOp"),FACE);
            var sketch = newSketch(context, id + "F52", { "sketchPlane" : qUnion([Q0])});
            skLineSegment(sketch, "E204", {"start": v(11.05, 13.24) * mm, "end": v(2.85, 0) * mm});
            skLineSegment(sketch, "E205", {"start": v(3.92, 1.72) * mm, "end": v(8.27, -0.97) * mm});
            skArc(sketch, "E206", {"start": v(8.27, -0.97) * mm, "mid": v(11.03, 5.87) * mm, "end": v(11.05, 13.24) * mm});
            skSolve(sketch);
        }
        {
            var Q0;
            Q0 = qSketchRegion(id + "F52", true);
            var Q1;
            Q1=sQuery(id+"F52.wireOp",EDGE,"E205");
            revolve(context, id + "F53", {"operationType" : NewBodyOperationType.ADD, "surfaceOperationType" : NewSurfaceOperationType.NEW, "entities" : qUnion([Q0]), "axis" : qUnion([Q1]), "revolveType" : RevolveType.FULL});
        }
        {
            var Q0;
            Q0=qCreatedBy(makeId("Right.planeOp"),FACE);
            var sketch = newSketch(context, id + "F54", { "sketchPlane" : qUnion([Q0])});
            skLineSegment(sketch, "E207", {"start": v(-2.92, 0) * mm, "end": v(-18.73, 9.75) * mm});
            skLineSegment(sketch, "E208", {"start": v(-6.25, 2.05) * mm, "end": v(-10.92, -5.52) * mm});
            skArc(sketch, "E209", {"start": v(-18.73, 9.75) * mm, "mid": v(-16.24, 1.39) * mm, "end": v(-10.92, -5.52) * mm});
            skSolve(sketch);
        }
        {
            var Q0;
            Q0 = qSketchRegion(id + "F54", true);
            var Q1;
            Q1=sQuery(id+"F54.wireOp",EDGE,"E208");
            revolve(context, id + "F55", {"operationType" : NewBodyOperationType.ADD, "surfaceOperationType" : NewSurfaceOperationType.NEW, "entities" : qUnion([Q0]), "axis" : qUnion([Q1]), "revolveType" : RevolveType.FULL});
        }
        {
            var Q0;
            Q0=qCreatedBy(makeId("Right.planeOp"),FACE);
            var sketch = newSketch(context, id + "F56", { "sketchPlane" : qUnion([Q0])});
            skLineSegment(sketch, "E210", {"start": v(0, -2.77) * mm, "end": v(17.43, 9.4) * mm});
            skLineSegment(sketch, "E211", {"start": v(6.12, 1.5) * mm, "end": v(11.06, -5.58) * mm});
            skArc(sketch, "E212", {"start": v(11.06, -5.58) * mm, "mid": v(15.76, 1.26) * mm, "end": v(17.43, 9.4) * mm});
            skSolve(sketch);
        }
        {
            var Q0;
            Q0 = qSketchRegion(id + "F56", true);
            var Q1;
            Q1=sQuery(id+"F56.wireOp",EDGE,"E211");
            revolve(context, id + "F57", {"operationType" : NewBodyOperationType.ADD, "surfaceOperationType" : NewSurfaceOperationType.NEW, "entities" : qUnion([Q0]), "axis" : qUnion([Q1]), "revolveType" : RevolveType.FULL});
        }
        {
            var Q0;
            Q0=qCreatedBy(makeId("Front.planeOp"),FACE);
            var sketch = newSketch(context, id + "F58", { "sketchPlane" : qUnion([Q0])});
            skLineSegment(sketch, "E213", {"start": v(2.28, 0) * mm, "end": v(17.2, 10.44) * mm});
            skLineSegment(sketch, "E214", {"start": v(7.99, 4) * mm, "end": v(12.73, -2.78) * mm});
            skArc(sketch, "E215", {"start": v(12.73, -2.78) * mm, "mid": v(16.68, 3.25) * mm, "end": v(17.2, 10.44) * mm});
            skSolve(sketch);
        }
        {
            var Q0;
            Q0 = qSketchRegion(id + "F58", true);
            var Q1;
            Q1=sQuery(id+"F58.wireOp",EDGE,"E214");
            revolve(context, id + "F59", {"operationType" : NewBodyOperationType.ADD, "surfaceOperationType" : NewSurfaceOperationType.NEW, "entities" : qUnion([Q0]), "axis" : qUnion([Q1]), "revolveType" : RevolveType.FULL});
        }
        {
            var Q0;
            Q0=qCreatedBy(makeId("Front.planeOp"),FACE);
            var sketch = newSketch(context, id + "F60", { "sketchPlane" : qUnion([Q0])});
            skLineSegment(sketch, "E216", {"start": v(-3.4, 0) * mm, "end": v(-18.52, 9.38) * mm});
            skLineSegment(sketch, "E217", {"start": v(-7.88, 2.77) * mm, "end": v(-11.8, -3.55) * mm});
            skArc(sketch, "E218", {"start": v(-18.52, 9.38) * mm, "mid": v(-16.76, 2.08) * mm, "end": v(-11.8, -3.55) * mm});
            skSolve(sketch);
        }
        {
            var Q0;
            Q0 = qSketchRegion(id + "F60", true);
            var Q1;
            Q1=sQuery(id+"F60.wireOp",EDGE,"E217");
            revolve(context, id + "F61", {"operationType" : NewBodyOperationType.ADD, "surfaceOperationType" : NewSurfaceOperationType.NEW, "entities" : qUnion([Q0]), "axis" : qUnion([Q1]), "revolveType" : RevolveType.FULL});
        }
        {
            var Q0;
            Q0=qCreatedBy(makeId("Right.planeOp"),FACE);
            var sketch = newSketch(context, id + "F62", { "sketchPlane" : qUnion([Q0])});
            skLineSegment(sketch, "E219", {"start": v(0, -3.7) * mm, "end": v(-23.8, 6.68) * mm});
            skLineSegment(sketch, "E220", {"start": v(-8.48, 0) * mm, "end": v(-11.04, -5.89) * mm});
            skArc(sketch, "E221", {"start": v(-23.8, 6.68) * mm, "mid": v(-18.75, -0.96) * mm, "end": v(-11.04, -5.89) * mm});
            skSolve(sketch);
        }
        {
            var Q0;
            Q0 = qSketchRegion(id + "F62", true);
            var Q1;
            Q1=sQuery(id+"F62.wireOp",EDGE,"E220");
            revolve(context, id + "F63", {"operationType" : NewBodyOperationType.ADD, "surfaceOperationType" : NewSurfaceOperationType.NEW, "entities" : qUnion([Q0]), "axis" : qUnion([Q1]), "revolveType" : RevolveType.FULL});
        }
        {
            var Q0;
            Q0=qCreatedBy(makeId("Right.planeOp"),FACE);
            var sketch = newSketch(context, id + "F64", { "sketchPlane" : qUnion([Q0])});
            skLineSegment(sketch, "E222", {"start": v(-4.4, -6.19) * mm, "end": v(23.7, 5.82) * mm});
            skLineSegment(sketch, "E223", {"start": v(9.65, -0.18) * mm, "end": v(12.36, -6.5) * mm});
            skArc(sketch, "E224", {"start": v(12.36, -6.5) * mm, "mid": v(19.72, -1.9) * mm, "end": v(23.7, 5.82) * mm});
            skSolve(sketch);
        }
        {
            var Q0;
            Q0 = qSketchRegion(id + "F64", true);
            var Q1;
            Q1=sQuery(id+"F64.wireOp",EDGE,"E223");
            revolve(context, id + "F65", {"operationType" : NewBodyOperationType.ADD, "surfaceOperationType" : NewSurfaceOperationType.NEW, "entities" : qUnion([Q0]), "axis" : qUnion([Q1]), "revolveType" : RevolveType.FULL});
        }
        {
            var Q0;
            Q0=qCreatedBy(makeId("Front.planeOp"),FACE);
            var sketch = newSketch(context, id + "F66", { "sketchPlane" : qUnion([Q0])});
            skLineSegment(sketch, "E225", {"start": v(-2.26, -6.84) * mm, "end": v(22.5, 7.1) * mm});
            skLineSegment(sketch, "E226", {"start": v(8.66, -0.7) * mm, "end": v(11.86, -6.37) * mm});
            skArc(sketch, "E227", {"start": v(11.86, -6.37) * mm, "mid": v(18.75, -0.88) * mm, "end": v(22.5, 7.1) * mm});
            skSolve(sketch);
        }
        {
            var Q0;
            Q0 = qSketchRegion(id + "F66", true);
            var Q1;
            Q1=sQuery(id+"F66.wireOp",EDGE,"E226");
            revolve(context, id + "F67", {"operationType" : NewBodyOperationType.ADD, "surfaceOperationType" : NewSurfaceOperationType.NEW, "entities" : qUnion([Q0]), "axis" : qUnion([Q1]), "revolveType" : RevolveType.FULL});
        }
        {
            var Q0;
            Q0=qCreatedBy(makeId("Front.planeOp"),FACE);
            var sketch = newSketch(context, id + "F68", { "sketchPlane" : qUnion([Q0])});
            skLineSegment(sketch, "E228", {"start": v(2.6, -7.53) * mm, "end": v(-23.95, 5.69) * mm});
            skLineSegment(sketch, "E229", {"start": v(-10.67, -0.92) * mm, "end": v(-13.09, -5.77) * mm});
            skArc(sketch, "E230", {"start": v(-23.95, 5.69) * mm, "mid": v(-19.85, -1.3) * mm, "end": v(-13.09, -5.77) * mm});
            skSolve(sketch);
        }
        {
            var Q0;
            Q0 = qSketchRegion(id + "F68", true);
            var Q1;
            Q1=sQuery(id+"F68.wireOp",EDGE,"E229");
            revolve(context, id + "F69", {"operationType" : NewBodyOperationType.ADD, "surfaceOperationType" : NewSurfaceOperationType.NEW, "entities" : qUnion([Q0]), "axis" : qUnion([Q1]), "revolveType" : RevolveType.FULL});
        }
        {
            var Q0;
            Q0=qCreatedBy(makeId("Right.planeOp"),FACE);
            var sketch = newSketch(context, id + "F70", { "sketchPlane" : qUnion([Q0])});
            skLineSegment(sketch, "E231", {"start": v(0, -9.5) * mm, "end": v(33.43, 0) * mm});
            skLineSegment(sketch, "E232", {"start": v(33.43, 0) * mm, "end": v(14.89, -5.27) * mm});
            skLineSegment(sketch, "E233", {"start": v(14.89, -5.27) * mm, "end": v(16.41, -10.64) * mm});
            skArc(sketch, "E234", {"start": v(16.41, -10.64) * mm, "mid": v(25.74, -6.63) * mm, "end": v(33.43, 0) * mm});
            skSolve(sketch);
        }
        {
            var Q0;
            Q0 = qSketchRegion(id + "F70", true);
            var Q1;
            Q1=sQuery(id+"F70.wireOp",EDGE,"E233");
            revolve(context, id + "F71", {"surfaceOperationType" : NewSurfaceOperationType.NEW, "entities" : qUnion([Q0]), "axis" : qUnion([Q1]), "revolveType" : RevolveType.FULL});
        }
        {
            var Q0;
            Q0=qCreatedBy(makeId("Right.planeOp"),FACE);
            var sketch = newSketch(context, id + "F72", { "sketchPlane" : qUnion([Q0])});
            skLineSegment(sketch, "E235", {"start": v(16, -5.02) * mm, "end": v(17.95, -4.23) * mm});
            skLineSegment(sketch, "E236", {"start": v(17.95, -4.23) * mm, "end": v(19.43, -3.93) * mm});
            skLineSegment(sketch, "E237", {"start": v(19.43, -3.93) * mm, "end": v(20.58, -3.46) * mm});
            skLineSegment(sketch, "E238", {"start": v(20.58, -3.46) * mm, "end": v(23.05, -3.46) * mm});
            skLineSegment(sketch, "E239", {"start": v(23.05, -3.46) * mm, "end": v(26.47, -3.12) * mm});
            skLineSegment(sketch, "E240", {"start": v(26.47, -3.12) * mm, "end": v(30.24, -1.58) * mm});
            skLineSegment(sketch, "E241", {"start": v(30.24, -1.58) * mm, "end": v(34.6, 0.64) * mm});
            skLineSegment(sketch, "E242", {"start": v(34.6, 0.64) * mm, "end": v(26.14, -8.73) * mm});
            skLineSegment(sketch, "E243", {"start": v(26.14, -8.73) * mm, "end": v(25.13, -7.82) * mm});
            skLineSegment(sketch, "E244", {"start": v(25.13, -7.82) * mm, "end": v(21.23, -9.41) * mm});
            skLineSegment(sketch, "E245", {"start": v(21.23, -9.41) * mm, "end": v(16.75, -10.23) * mm});
            skLineSegment(sketch, "E246", {"start": v(16.75, -10.23) * mm, "end": v(12.35, -10.23) * mm});
            skLineSegment(sketch, "E247", {"start": v(12.35, -10.23) * mm, "end": v(2.47, -10.23) * mm});
            skLineSegment(sketch, "E248", {"start": v(2.47, -10.23) * mm, "end": v(-0.45, -9.77) * mm});
            skLineSegment(sketch, "E249", {"start": v(-0.45, -9.77) * mm, "end": v(-3.14, -9.77) * mm});
            skLineSegment(sketch, "E250", {"start": v(-3.14, -9.77) * mm, "end": v(-5.46, -11.2) * mm});
            skLineSegment(sketch, "E251", {"start": v(-5.46, -11.2) * mm, "end": v(1.5, -13.2) * mm});
            skLineSegment(sketch, "E252", {"start": v(1.5, -13.2) * mm, "end": v(20.09, -12.08) * mm});
            skLineSegment(sketch, "E253", {"start": v(20.09, -12.08) * mm, "end": v(34.74, -6.75) * mm});
            skLineSegment(sketch, "E254", {"start": v(34.74, -6.75) * mm, "end": v(37.7, 0.53) * mm});
            skLineSegment(sketch, "E255", {"start": v(37.7, 0.53) * mm, "end": v(33.26, 1.18) * mm});
            skLineSegment(sketch, "E256", {"start": v(33.26, 1.18) * mm, "end": v(19.43, -3.18) * mm});
            skLineSegment(sketch, "E257", {"start": v(19.43, -3.18) * mm, "end": v(15.92, -4.97) * mm});
            skLineSegment(sketch, "E258", {"start": v(15.92, -4.97) * mm, "end": v(15.85, -5) * mm});
            skLineSegment(sketch, "E259", {"start": v(15.85, -5) * mm, "end": v(15.98, -4.97) * mm});
            skLineSegment(sketch, "E260", {"start": v(15.98, -4.97) * mm, "end": v(16.51, -4.81) * mm});
            skSolve(sketch);
        }
        {
            var Q0;
            Q0 = qSketchRegion(id + "F72", true);
            extrude(context, id + "F73", {"entities" : qUnion([Q0]), "operationType" : NewBodyOperationType.REMOVE, "oppositeDirection" : true, "depth" : 25.4 * mm, "offsetDistance" : 25.4 * mm});
        }
        {
            var Q0;
            Q0 = qSketchRegion(id + "F72", true);
            extrude(context, id + "F74", {"entities" : qUnion([Q0]), "operationType" : NewBodyOperationType.REMOVE, "depth" : 25.4 * mm, "offsetDistance" : 25.4 * mm});
        }
        {
            var Q0;
            Q0=qCreatedBy(makeId("Top.planeOp"),FACE);
            var sketch = newSketch(context, id + "F75", { "sketchPlane" : qUnion([Q0])});
            skLineSegment(sketch, "E261", {"start": v(12.09, 13.09) * mm, "end": v(28.12, 29.12) * mm});
            skSolve(sketch);
        }
        {
            var Q0;
            Q0=sQuery(id+"F75.wireOp",EDGE,"E261");
            cPlane(context, id + "F76", {"entities" : qUnion([Q0]), "cplaneType" : CPlaneType.LINE_ANGLE, "offset" : 25.4 * mm, "angle" : 90 * degree, "width" : 152.4 * mm, "height" : 152.4 * mm});
        }
        {
            var Q0;
            Q0=qCreatedBy(id+"F76.planeOp",FACE);
            var sketch = newSketch(context, id + "F77", { "sketchPlane" : qUnion([Q0])});
            skLineSegment(sketch, "E262", {"start": v(12.21, -6.2) * mm, "end": v(40.63, 0) * mm});
            skLineSegment(sketch, "E263", {"start": v(40.63, 0) * mm, "end": v(26.42, -3.1) * mm});
            skLineSegment(sketch, "E264", {"start": v(26.42, -3.1) * mm, "end": v(27.9, -9.85) * mm});
            skArc(sketch, "E265", {"start": v(27.9, -9.85) * mm, "mid": v(34.87, -5.71) * mm, "end": v(40.63, 0) * mm});
            skSolve(sketch);
        }
        {
            var Q0;
            Q0 = qSketchRegion(id + "F77", true);
            var Q1;
            Q1=sQuery(id+"F77.wireOp",EDGE,"E264");
            revolve(context, id + "F78", {"surfaceOperationType" : NewSurfaceOperationType.NEW, "entities" : qUnion([Q0]), "axis" : qUnion([Q1]), "revolveType" : RevolveType.FULL});
        }
        {
            var Q0;
            Q0=qCreatedBy(id+"F76.planeOp",FACE);
            var sketch = newSketch(context, id + "F79", { "sketchPlane" : qUnion([Q0])});
            skLineSegment(sketch, "E266", {"start": v(22.58, -3.62) * mm, "end": v(25.85, -2.68) * mm});
            skLineSegment(sketch, "E267", {"start": v(25.85, -2.68) * mm, "end": v(28.45, -2.68) * mm});
            skLineSegment(sketch, "E268", {"start": v(28.45, -2.68) * mm, "end": v(32.76, -2.68) * mm});
            skLineSegment(sketch, "E269", {"start": v(32.76, -2.68) * mm, "end": v(36.81, -1.45) * mm});
            skLineSegment(sketch, "E270", {"start": v(36.81, -1.45) * mm, "end": v(42.04, 0.62) * mm});
            skLineSegment(sketch, "E271", {"start": v(42.04, 0.62) * mm, "end": v(39.14, -3.36) * mm});
            skLineSegment(sketch, "E272", {"start": v(39.14, -3.36) * mm, "end": v(32.5, -7.34) * mm});
            skLineSegment(sketch, "E273", {"start": v(32.5, -7.34) * mm, "end": v(24.33, -9.17) * mm});
            skLineSegment(sketch, "E274", {"start": v(24.33, -9.17) * mm, "end": v(18.84, -9.17) * mm});
            skLineSegment(sketch, "E275", {"start": v(18.84, -9.17) * mm, "end": v(18.84, -10.93) * mm});
            skLineSegment(sketch, "E276", {"start": v(18.84, -10.93) * mm, "end": v(31.44, -10.93) * mm});
            skLineSegment(sketch, "E277", {"start": v(31.44, -10.93) * mm, "end": v(41.38, -3.58) * mm});
            skLineSegment(sketch, "E278", {"start": v(41.38, -3.58) * mm, "end": v(44.26, 1.66) * mm});
            skLineSegment(sketch, "E279", {"start": v(44.26, 1.66) * mm, "end": v(37.4, 2.89) * mm});
            skLineSegment(sketch, "E280", {"start": v(37.4, 2.89) * mm, "end": v(22.58, -3.62) * mm});
            skSolve(sketch);
        }
        {
            var Q0;
            Q0 = qSketchRegion(id + "F79", true);
            extrude(context, id + "F80", {"entities" : qUnion([Q0]), "operationType" : NewBodyOperationType.REMOVE, "oppositeDirection" : true, "depth" : 25.4 * mm, "offsetDistance" : 25.4 * mm});
        }
        {
            var Q0;
            Q0 = qSketchRegion(id + "F79", true);
            extrude(context, id + "F81", {"entities" : qUnion([Q0]), "operationType" : NewBodyOperationType.REMOVE, "depth" : 25.4 * mm, "offsetDistance" : 25.4 * mm});
        }
        {
            var Q0;
            Q0=makeQuery(id+"F78.opRevolve","SWEPT_BODY",BODY,{"disambiguationData":[OSD([sQuery(id+"F77.wireOp",EDGE,"E263"),sQuery(id+"F77.wireOp",EDGE,"E264"),sQuery(id+"F77.wireOp",EDGE,"E265")])]});
            transform(context, id + "F82", {"entities" : qUnion([Q0]), "transformType" : TransformType.TRANSLATION_3D, "dx" : -0.25 * mm, "dy" : -6.1 * mm, "dz" : 0 * mm, "makeCopy" : false});
        }
        {
            var Q0;
            Q0=qCreatedBy(makeId("Top.planeOp"),FACE);
            var sketch = newSketch(context, id + "F83", { "sketchPlane" : qUnion([Q0])});
            skLineSegment(sketch, "E281", {"start": v(22.6, -0.95) * mm, "end": v(26.24, 2.22) * mm});
            skLineSegment(sketch, "E282", {"start": v(26.24, 2.22) * mm, "end": v(28.67, 7.17) * mm});
            skLineSegment(sketch, "E283", {"start": v(28.67, 7.17) * mm, "end": v(28.67, 10.71) * mm});
            skLineSegment(sketch, "E284", {"start": v(28.67, 10.71) * mm, "end": v(28.67, 15.94) * mm});
            skLineSegment(sketch, "E285", {"start": v(28.67, 15.94) * mm, "end": v(28.67, 19.76) * mm});
            skLineSegment(sketch, "E286", {"start": v(28.67, 19.76) * mm, "end": v(28.67, 22.84) * mm});
            skLineSegment(sketch, "E287", {"start": v(28.67, 22.84) * mm, "end": v(24.37, 23.59) * mm});
            skLineSegment(sketch, "E288", {"start": v(24.37, 23.59) * mm, "end": v(18.96, 23.59) * mm});
            skLineSegment(sketch, "E289", {"start": v(18.96, 23.59) * mm, "end": v(15.5, 24.8) * mm});
            skLineSegment(sketch, "E290", {"start": v(15.5, 24.8) * mm, "end": v(9.54, 24.8) * mm});
            skLineSegment(sketch, "E291", {"start": v(9.54, 24.8) * mm, "end": v(14.76, 28.07) * mm});
            skLineSegment(sketch, "E292", {"start": v(14.76, 28.07) * mm, "end": v(35.76, 27.04) * mm});
            skLineSegment(sketch, "E293", {"start": v(35.76, 27.04) * mm, "end": v(35.94, 12.49) * mm});
            skLineSegment(sketch, "E294", {"start": v(35.94, 12.49) * mm, "end": v(28.57, -1.51) * mm});
            skLineSegment(sketch, "E295", {"start": v(28.57, -1.51) * mm, "end": v(22.6, -0.95) * mm});
            skSolve(sketch);
        }
        {
            var Q0;
            Q0 = qSketchRegion(id + "F83", true);
            extrude(context, id + "F84", {"entities" : qUnion([Q0]), "operationType" : NewBodyOperationType.REMOVE, "oppositeDirection" : true, "depth" : 25.4 * mm, "offsetDistance" : 25.4 * mm});
        }
        {
            var Q0;
            Q0 = qSketchRegion(id + "F72", true);
            extrude(context, id + "F85", {"entities" : qUnion([Q0]), "operationType" : NewBodyOperationType.REMOVE, "oppositeDirection" : true, "depth" : 25.4 * mm, "offsetDistance" : 25.4 * mm});
        }
        {
            var Q0;
            Q0 = qSketchRegion(id + "F72", true);
            extrude(context, id + "F86", {"entities" : qUnion([Q0]), "operationType" : NewBodyOperationType.REMOVE, "depth" : 12.7 * mm, "offsetDistance" : 25.4 * mm});
        }
        {
            var Q0;
            Q0=qCreatedBy(makeId("Top.planeOp"),FACE);
            var sketch = newSketch(context, id + "F87", { "sketchPlane" : qUnion([Q0])});
            skLineSegment(sketch, "E296", {"start": v(-17.64, 12.5) * mm, "end": v(-17.64, 16.78) * mm});
            skLineSegment(sketch, "E297", {"start": v(-17.64, 16.78) * mm, "end": v(-15.64, 21.5) * mm});
            skLineSegment(sketch, "E298", {"start": v(-15.64, 21.5) * mm, "end": v(-10.64, 26.15) * mm});
            skLineSegment(sketch, "E299", {"start": v(-10.64, 26.15) * mm, "end": v(-3.83, 30.34) * mm});
            skLineSegment(sketch, "E300", {"start": v(-3.83, 30.34) * mm, "end": v(0, 33.37) * mm});
            skLineSegment(sketch, "E301", {"start": v(0, 33.37) * mm, "end": v(3.07, 30.47) * mm});
            skLineSegment(sketch, "E302", {"start": v(3.07, 30.47) * mm, "end": v(7.42, 28.37) * mm});
            skLineSegment(sketch, "E303", {"start": v(7.42, 28.37) * mm, "end": v(11.11, 24.58) * mm});
            skLineSegment(sketch, "E304", {"start": v(11.11, 24.58) * mm, "end": v(14, 24.58) * mm});
            skLineSegment(sketch, "E305", {"start": v(14, 24.58) * mm, "end": v(18.5, 23.62) * mm});
            skLineSegment(sketch, "E306", {"start": v(18.5, 23.62) * mm, "end": v(20.82, 23.62) * mm});
            skLineSegment(sketch, "E307", {"start": v(20.82, 23.62) * mm, "end": v(4.05, 38.38) * mm});
            skLineSegment(sketch, "E308", {"start": v(4.05, 38.38) * mm, "end": v(-13.04, 35.33) * mm});
            skLineSegment(sketch, "E309", {"start": v(-13.04, 35.33) * mm, "end": v(-22.9, 14.55) * mm});
            skLineSegment(sketch, "E310", {"start": v(-22.9, 14.55) * mm, "end": v(-18.96, 11.58) * mm});
            skLineSegment(sketch, "E311", {"start": v(-18.96, 11.58) * mm, "end": v(-18.47, 12) * mm});
            skLineSegment(sketch, "E312", {"start": v(-18.47, 12) * mm, "end": v(-17.82, 12.5) * mm});
            skLineSegment(sketch, "E313", {"start": v(-17.82, 12.5) * mm, "end": v(-17.64, 12.6) * mm});
            skSolve(sketch);
        }
        {
            var Q0;
            Q0 = qSketchRegion(id + "F87", true);
            extrude(context, id + "F88", {"entities" : qUnion([Q0]), "operationType" : NewBodyOperationType.REMOVE, "oppositeDirection" : true, "depth" : 25.4 * mm, "offsetDistance" : 25.4 * mm});
        }
        {
            var Q0;
            Q0=qCreatedBy(makeId("Right.planeOp"),FACE);
            var sketch = newSketch(context, id + "F89", { "sketchPlane" : qUnion([Q0])});
            skLineSegment(sketch, "E314", {"start": v(0, -9.77) * mm, "end": v(-32.75, 0) * mm});
            skLineSegment(sketch, "E315", {"start": v(-16.38, -4.88) * mm, "end": v(-17.81, -9.7) * mm});
            skArc(sketch, "E316", {"start": v(-32.75, 0) * mm, "mid": v(-26.01, -5.97) * mm, "end": v(-17.81, -9.7) * mm});
            skSolve(sketch);
        }
        {
            var Q0;
            Q0 = qSketchRegion(id + "F89", true);
            var Q1;
            Q1=sQuery(id+"F89.wireOp",EDGE,"E315");
            revolve(context, id + "F90", {"surfaceOperationType" : NewSurfaceOperationType.NEW, "entities" : qUnion([Q0]), "axis" : qUnion([Q1]), "revolveType" : RevolveType.FULL});
        }
        {
            var Q0;
            Q0=qCreatedBy(makeId("Top.planeOp"),FACE);
            var sketch = newSketch(context, id + "F91", { "sketchPlane" : qUnion([Q0])});
            skLineSegment(sketch, "E317", {"start": v(16.7, -13.02) * mm, "end": v(16.7, -17.8) * mm});
            skLineSegment(sketch, "E318", {"start": v(16.7, -17.8) * mm, "end": v(15.43, -21) * mm});
            skLineSegment(sketch, "E319", {"start": v(15.43, -21) * mm, "end": v(11.92, -25.95) * mm});
            skLineSegment(sketch, "E320", {"start": v(11.92, -25.95) * mm, "end": v(5.93, -29.78) * mm});
            skLineSegment(sketch, "E321", {"start": v(5.93, -29.78) * mm, "end": v(0, -32.57) * mm});
            skLineSegment(sketch, "E322", {"start": v(0, -32.57) * mm, "end": v(-5.32, -29.94) * mm});
            skLineSegment(sketch, "E323", {"start": v(-5.32, -29.94) * mm, "end": v(-12.34, -26.1) * mm});
            skLineSegment(sketch, "E324", {"start": v(-12.34, -26.1) * mm, "end": v(-16.65, -20.36) * mm});
            skLineSegment(sketch, "E325", {"start": v(-16.65, -20.36) * mm, "end": v(-17.21, -15.25) * mm});
            skLineSegment(sketch, "E326", {"start": v(-17.21, -15.25) * mm, "end": v(-16.77, -13.2) * mm});
            skLineSegment(sketch, "E327", {"start": v(-16.77, -13.2) * mm, "end": v(-19.31, -14.34) * mm});
            skLineSegment(sketch, "E328", {"start": v(-19.31, -14.34) * mm, "end": v(-22.8, -19.42) * mm});
            skLineSegment(sketch, "E329", {"start": v(-22.8, -19.42) * mm, "end": v(-13.19, -35) * mm});
            skLineSegment(sketch, "E330", {"start": v(-13.19, -35) * mm, "end": v(4.13, -40.77) * mm});
            skLineSegment(sketch, "E331", {"start": v(4.13, -40.77) * mm, "end": v(21.44, -24.8) * mm});
            skLineSegment(sketch, "E332", {"start": v(21.44, -24.8) * mm, "end": v(16.7, -13.02) * mm});
            skSolve(sketch);
        }
        {
            var Q0;
            Q0 = qSketchRegion(id + "F91", true);
            extrude(context, id + "F92", {"entities" : qUnion([Q0]), "operationType" : NewBodyOperationType.REMOVE, "oppositeDirection" : true, "depth" : 25.4 * mm, "offsetDistance" : 25.4 * mm});
        }
        {
            var Q0;
            Q0=qCreatedBy(makeId("Right.planeOp"),FACE);
            var sketch = newSketch(context, id + "F93", { "sketchPlane" : qUnion([Q0])});
            skLineSegment(sketch, "E333", {"start": v(-11.75, -6.1) * mm, "end": v(-15.9, -4.99) * mm});
            skLineSegment(sketch, "E334", {"start": v(-15.9, -4.99) * mm, "end": v(-22.89, -3.78) * mm});
            skLineSegment(sketch, "E335", {"start": v(-22.89, -3.78) * mm, "end": v(-27.72, -2.48) * mm});
            skLineSegment(sketch, "E336", {"start": v(-27.72, -2.48) * mm, "end": v(-33.68, 0.71) * mm});
            skLineSegment(sketch, "E337", {"start": v(-33.68, 0.71) * mm, "end": v(-25.3, -7.75) * mm});
            skLineSegment(sketch, "E338", {"start": v(-25.3, -7.75) * mm, "end": v(-19.7, -9.3) * mm});
            skLineSegment(sketch, "E339", {"start": v(-19.7, -9.3) * mm, "end": v(-14.34, -10.42) * mm});
            skLineSegment(sketch, "E340", {"start": v(-14.34, -10.42) * mm, "end": v(0, -10.42) * mm});
            skLineSegment(sketch, "E341", {"start": v(0, -10.42) * mm, "end": v(-6.75, -15.09) * mm});
            skLineSegment(sketch, "E342", {"start": v(-6.75, -15.09) * mm, "end": v(-33.6, -14.4) * mm});
            skLineSegment(sketch, "E343", {"start": v(-33.6, -14.4) * mm, "end": v(-37.4, 2.52) * mm});
            skLineSegment(sketch, "E344", {"start": v(-37.4, 2.52) * mm, "end": v(-31.08, 3.94) * mm});
            skLineSegment(sketch, "E345", {"start": v(-31.08, 3.94) * mm, "end": v(-11.75, -6.1) * mm});
            skSolve(sketch);
        }
        {
            var Q0;
            Q0 = qSketchRegion(id + "F93", true);
            extrude(context, id + "F94", {"entities" : qUnion([Q0]), "operationType" : NewBodyOperationType.REMOVE, "oppositeDirection" : true, "depth" : 25.4 * mm, "offsetDistance" : 25.4 * mm});
        }
        {
            var Q0;
            Q0 = qSketchRegion(id + "F93", true);
            extrude(context, id + "F95", {"entities" : qUnion([Q0]), "operationType" : NewBodyOperationType.REMOVE, "depth" : 25.4 * mm, "offsetDistance" : 25.4 * mm});
        }
        {
            var Q0;
            Q0=qCreatedBy(makeId("Top.planeOp"),FACE);
            var sketch = newSketch(context, id + "F96", { "sketchPlane" : qUnion([Q0])});
            skLineSegment(sketch, "E346", {"start": v(-16.34, -12.98) * mm, "end": v(-31.91, -27.33) * mm});
            skSolve(sketch);
        }
        {
            var Q0;
            Q0=sQuery(id+"F96.wireOp",EDGE,"E346");
            cPlane(context, id + "F97", {"entities" : qUnion([Q0]), "cplaneType" : CPlaneType.LINE_ANGLE, "offset" : 25.4 * mm, "angle" : 0 * degree, "width" : 152.4 * mm, "height" : 152.4 * mm});
        }
        {
            var Q0;
            Q0=qCreatedBy(id+"F97.planeOp",FACE);
            var sketch = newSketch(context, id + "F98", { "sketchPlane" : qUnion([Q0])});
            skLineSegment(sketch, "E347", {"start": v(-3.09, -9.76) * mm, "end": v(-41.94, 0) * mm});
            skLineSegment(sketch, "E348", {"start": v(-24.07, -4.49) * mm, "end": v(-25.14, -8.74) * mm});
            skArc(sketch, "E349", {"start": v(-41.94, 0) * mm, "mid": v(-34.37, -5.97) * mm, "end": v(-25.14, -8.74) * mm});
            skSolve(sketch);
        }
        {
            var Q0;
            Q0 = qSketchRegion(id + "F98", true);
            var Q1;
            Q1=sQuery(id+"F98.wireOp",EDGE,"E348");
            revolve(context, id + "F99", {"operationType" : NewBodyOperationType.ADD, "surfaceOperationType" : NewSurfaceOperationType.NEW, "entities" : qUnion([Q0]), "axis" : qUnion([Q1]), "revolveType" : RevolveType.FULL});
        }
        {
            var Q0;
            Q0=qCreatedBy(makeId("Top.planeOp"),FACE);
            var sketch = newSketch(context, id + "F100", { "sketchPlane" : qUnion([Q0])});
            skLineSegment(sketch, "E350", {"start": v(-8.29, -21.56) * mm, "end": v(-10.98, -25.47) * mm});
            skLineSegment(sketch, "E351", {"start": v(-23.92, 1.4) * mm, "end": v(-23.76, 2.75) * mm});
            skLineSegment(sketch, "E352", {"start": v(-23.76, 2.75) * mm, "end": v(-27.79, 2.3) * mm});
            skLineSegment(sketch, "E353", {"start": v(-27.79, 2.3) * mm, "end": v(-45.39, -1.7) * mm});
            skLineSegment(sketch, "E354", {"start": v(-45.39, -1.7) * mm, "end": v(-37.18, -37.88) * mm});
            skLineSegment(sketch, "E355", {"start": v(-37.18, -37.88) * mm, "end": v(-16.7, -40.53) * mm});
            skLineSegment(sketch, "E356", {"start": v(-16.7, -40.53) * mm, "end": v(-6.74, -29.18) * mm});
            skLineSegment(sketch, "E357", {"start": v(-6.74, -29.18) * mm, "end": v(-8.13, -28.4) * mm});
            skLineSegment(sketch, "E358", {"start": v(-8.13, -28.4) * mm, "end": v(-10.32, -27.22) * mm});
            skLineSegment(sketch, "E359", {"start": v(-10.32, -27.22) * mm, "end": v(-11.93, -26.33) * mm});
            skLineSegment(sketch, "E360", {"start": v(-11.93, -26.33) * mm, "end": v(-12.15, -26.07) * mm});
            skLineSegment(sketch, "E361", {"start": v(-28.1, -26.16) * mm, "end": v(-30.66, -26.16) * mm});
            skLineSegment(sketch, "E362", {"start": v(-30.66, -26.16) * mm, "end": v(-31.14, -21.78) * mm});
            skLineSegment(sketch, "E363", {"start": v(-31.14, -21.78) * mm, "end": v(-31.8, -17.3) * mm});
            skLineSegment(sketch, "E364", {"start": v(-10.98, -25.47) * mm, "end": v(-12.15, -26.07) * mm});
            skLineSegment(sketch, "E365", {"start": v(-12.15, -26.07) * mm, "end": v(-14.4, -26.74) * mm});
            skLineSegment(sketch, "E366", {"start": v(-14.4, -26.74) * mm, "end": v(-18.11, -27.57) * mm});
            skLineSegment(sketch, "E367", {"start": v(-18.11, -27.57) * mm, "end": v(-22.9, -27) * mm});
            skLineSegment(sketch, "E368", {"start": v(-28.1, -26.16) * mm, "end": v(-22.9, -27) * mm});
            skLineSegment(sketch, "E369", {"start": v(-31.8, -17.3) * mm, "end": v(-31.8, -12.85) * mm});
            skLineSegment(sketch, "E370", {"start": v(-31.8, -12.85) * mm, "end": v(-31, -8.46) * mm});
            skLineSegment(sketch, "E371", {"start": v(-31, -8.46) * mm, "end": v(-28.5, -5.26) * mm});
            skLineSegment(sketch, "E372", {"start": v(-28.5, -5.26) * mm, "end": v(-25.64, -2.4) * mm});
            skLineSegment(sketch, "E373", {"start": v(-25.64, -2.4) * mm, "end": v(-23.87, -1.6) * mm});
            skLineSegment(sketch, "E374", {"start": v(-23.87, -1.6) * mm, "end": v(-23.9, -1.28) * mm});
            skLineSegment(sketch, "E375", {"start": v(-23.9, -1.28) * mm, "end": v(-23.92, -0.88) * mm});
            skLineSegment(sketch, "E376", {"start": v(-23.92, -0.88) * mm, "end": v(-23.92, 1.4) * mm});
            skSolve(sketch);
        }
        {
            var Q0;
            Q0 = qSketchRegion(id + "F100", true);
            extrude(context, id + "F101", {"entities" : qUnion([Q0]), "operationType" : NewBodyOperationType.REMOVE, "oppositeDirection" : true, "depth" : 25.4 * mm, "offsetDistance" : 25.4 * mm});
        }
        {
            var Q0;
            Q0=qCreatedBy(id+"F97.planeOp",FACE);
            var sketch = newSketch(context, id + "F102", { "sketchPlane" : qUnion([Q0])});
            skLineSegment(sketch, "E377", {"start": v(-14.14, -5.87) * mm, "end": v(-24.06, -3.72) * mm});
            skLineSegment(sketch, "E378", {"start": v(-24.06, -3.72) * mm, "end": v(-28.11, -3) * mm});
            skLineSegment(sketch, "E379", {"start": v(-28.11, -3) * mm, "end": v(-32.58, -3) * mm});
            skLineSegment(sketch, "E380", {"start": v(-32.58, -3) * mm, "end": v(-39.3, -1.95) * mm});
            skLineSegment(sketch, "E381", {"start": v(-39.3, -1.95) * mm, "end": v(-41.64, -0.71) * mm});
            skLineSegment(sketch, "E382", {"start": v(-41.64, -0.71) * mm, "end": v(-35.4, -7.92) * mm});
            skLineSegment(sketch, "E383", {"start": v(-35.4, -7.92) * mm, "end": v(-33.14, -7.92) * mm});
            skLineSegment(sketch, "E384", {"start": v(-33.14, -7.92) * mm, "end": v(-25.87, -9.39) * mm});
            skLineSegment(sketch, "E385", {"start": v(-25.87, -9.39) * mm, "end": v(-20.46, -10.05) * mm});
            skLineSegment(sketch, "E386", {"start": v(-20.46, -10.05) * mm, "end": v(-7.83, -9.21) * mm});
            skLineSegment(sketch, "E387", {"start": v(-7.83, -9.21) * mm, "end": v(-7.33, -16.74) * mm});
            skLineSegment(sketch, "E388", {"start": v(-7.33, -16.74) * mm, "end": v(-41.92, -14.98) * mm});
            skLineSegment(sketch, "E389", {"start": v(-41.92, -14.98) * mm, "end": v(-45.34, 2.43) * mm});
            skLineSegment(sketch, "E390", {"start": v(-45.34, 2.43) * mm, "end": v(-40.46, 1.45) * mm});
            skLineSegment(sketch, "E391", {"start": v(-40.46, 1.45) * mm, "end": v(-28.11, -3) * mm});
            skSolve(sketch);
        }
        {
            var Q0;
            Q0 = qSketchRegion(id + "F102", true);
            extrude(context, id + "F103", {"entities" : qUnion([Q0]), "operationType" : NewBodyOperationType.REMOVE, "oppositeDirection" : true, "depth" : 25.4 * mm, "offsetDistance" : 25.4 * mm});
        }
        {
            var Q0;
            Q0 = qSketchRegion(id + "F102", true);
            extrude(context, id + "F104", {"entities" : qUnion([Q0]), "operationType" : NewBodyOperationType.REMOVE, "depth" : 12.7 * mm, "offsetDistance" : 25.4 * mm});
        }
        {
            var Q0;
            Q0=qCreatedBy(makeId("Right.planeOp"),FACE);
            var sketch = newSketch(context, id + "F105", { "sketchPlane" : qUnion([Q0])});
            skLineSegment(sketch, "E392", {"start": v(21.02, -10.3) * mm, "end": v(-21.5, -10.3) * mm});
            skLineSegment(sketch, "E393", {"start": v(-21.5, -10.3) * mm, "end": v(-21.5, -14.37) * mm});
            skLineSegment(sketch, "E394", {"start": v(-21.5, -14.37) * mm, "end": v(18.5, -14.37) * mm});
            skLineSegment(sketch, "E395", {"start": v(18.5, -14.37) * mm, "end": v(21.02, -10.3) * mm});
            skSolve(sketch);
        }
        {
            var Q0;
            Q0 = qSketchRegion(id + "F105", true);
            extrude(context, id + "F106", {"entities" : qUnion([Q0]), "operationType" : NewBodyOperationType.REMOVE, "oppositeDirection" : true, "depth" : 50.8 * mm, "offsetDistance" : 25.4 * mm});
        }
        {
            var Q0;
            Q0 = qSketchRegion(id + "F105", true);
            extrude(context, id + "F107", {"entities" : qUnion([Q0]), "operationType" : NewBodyOperationType.REMOVE, "depth" : 25.4 * mm, "offsetDistance" : 25.4 * mm});
        }
        {
            var Q0;
            Q0=qCreatedBy(id+"F97.planeOp",FACE);
            var sketch = newSketch(context, id + "F108", { "sketchPlane" : qUnion([Q0])});
            skLineSegment(sketch, "E396", {"start": v(-14.26, -6.43) * mm, "end": v(-17.4, -5.7) * mm});
            skLineSegment(sketch, "E397", {"start": v(-17.4, -5.7) * mm, "end": v(-19.6, -5.34) * mm});
            skLineSegment(sketch, "E398", {"start": v(-19.6, -5.34) * mm, "end": v(-25.24, -4.01) * mm});
            skLineSegment(sketch, "E399", {"start": v(-25.24, -4.01) * mm, "end": v(-29.87, -3.6) * mm});
            skLineSegment(sketch, "E400", {"start": v(-34.57, -2.16) * mm, "end": v(-29.28, -2.77) * mm});
            skLineSegment(sketch, "E401", {"start": v(-29.28, -2.77) * mm, "end": v(-25.26, -3.74) * mm});
            skLineSegment(sketch, "E402", {"start": v(-25.26, -3.74) * mm, "end": v(-24.07, -4.04) * mm});
            skLineSegment(sketch, "E403", {"start": v(-24.07, -4.04) * mm, "end": v(-20.15, -5) * mm});
            skLineSegment(sketch, "E404", {"start": v(-20.15, -5) * mm, "end": v(-18.35, -5.48) * mm});
            skLineSegment(sketch, "E405", {"start": v(-18.35, -5.48) * mm, "end": v(-17.4, -5.7) * mm});
            skLineSegment(sketch, "E406", {"start": v(-29.87, -3.6) * mm, "end": v(-32.29, -3.33) * mm});
            skLineSegment(sketch, "E407", {"start": v(-32.29, -3.33) * mm, "end": v(-34.68, -2.76) * mm});
            skLineSegment(sketch, "E408", {"start": v(-34.68, -2.76) * mm, "end": v(-37.14, -2.14) * mm});
            skLineSegment(sketch, "E409", {"start": v(-37.14, -2.14) * mm, "end": v(-34.57, -2.16) * mm});
            skSolve(sketch);
        }
        {
            var Q0;
            Q0 = qSketchRegion(id + "F108", true);
            extrude(context, id + "F109", {"entities" : qUnion([Q0]), "operationType" : NewBodyOperationType.REMOVE, "oppositeDirection" : true, "depth" : 25.4 * mm, "offsetDistance" : 25.4 * mm});
        }
        {
            var Q0;
            Q0 = qSketchRegion(id + "F108", true);
            extrude(context, id + "F110", {"entities" : qUnion([Q0]), "operationType" : NewBodyOperationType.REMOVE, "depth" : 12.7 * mm, "offsetDistance" : 25.4 * mm});
        }
        {
            var Q0;
            Q0=qCreatedBy(makeId("Top.planeOp"),FACE);
            var sketch = newSketch(context, id + "F111", { "sketchPlane" : qUnion([Q0])});
            skLineSegment(sketch, "E410", {"start": v(10.48, 0) * mm, "end": v(10.48, 3) * mm});
            skLineSegment(sketch, "E411", {"start": v(10.48, 3) * mm, "end": v(-10.78, 3) * mm});
            skLineSegment(sketch, "E412", {"start": v(-10.78, 3) * mm, "end": v(-10.78, -0.77) * mm});
            skLineSegment(sketch, "E413", {"start": v(3.95, -12.89) * mm, "end": v(6.4, -1.66) * mm});
            skLineSegment(sketch, "E414", {"start": v(6.4, -1.66) * mm, "end": v(9.99, -1.66) * mm});
            skLineSegment(sketch, "E415", {"start": v(9.99, -1.66) * mm, "end": v(10.48, 0) * mm});
            skLineSegment(sketch, "E416", {"start": v(-10.78, -0.77) * mm, "end": v(-14.95, -3.76) * mm});
            skLineSegment(sketch, "E417", {"start": v(-14.95, -3.76) * mm, "end": v(-14.43, -6.1) * mm});
            skLineSegment(sketch, "E418", {"start": v(-14.43, -6.1) * mm, "end": v(-6.89, -14.42) * mm});
            skLineSegment(sketch, "E419", {"start": v(-6.89, -14.42) * mm, "end": v(3.95, -12.89) * mm});
            skSolve(sketch);
        }
        {
            var Q0;
            Q0 = qSketchRegion(id + "F111", true);
            extrude(context, id + "F112", {"entities" : qUnion([Q0]), "oppositeDirection" : true, "depth" : 10.16 * mm, "offsetDistance" : 25.4 * mm});
        }
    });
